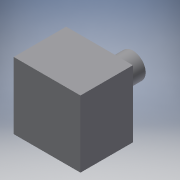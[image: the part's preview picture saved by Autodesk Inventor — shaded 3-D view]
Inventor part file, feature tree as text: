
AUTODESK INVENTOR PART (.ipt)
format: ipt  version: 2018 (Build 220112000, 112)  size: 95,232 bytes
history: native  units: mm
features: extrude x2, sketch x2
ambient origin geometry x8: Origin, YZ Plane, XZ Plane, XY Plane, X Axis, Y Axis, Z Axis, Center Point
bodies: Solid1 (feature_tree)
feature tree (4):
  extrude  "Extrusion1"  Depth=42.0mm
  extrude  "Extrusion2"  Depth=21.0mm
  sketch  "Sketch1"  dims[d0=42.0mm d1=42.0mm]
  sketch  "Sketch2"  dims[d2=33.0mm d3=0.0mm d4=16.0mm d5=21.0mm d6=0.0mm]
